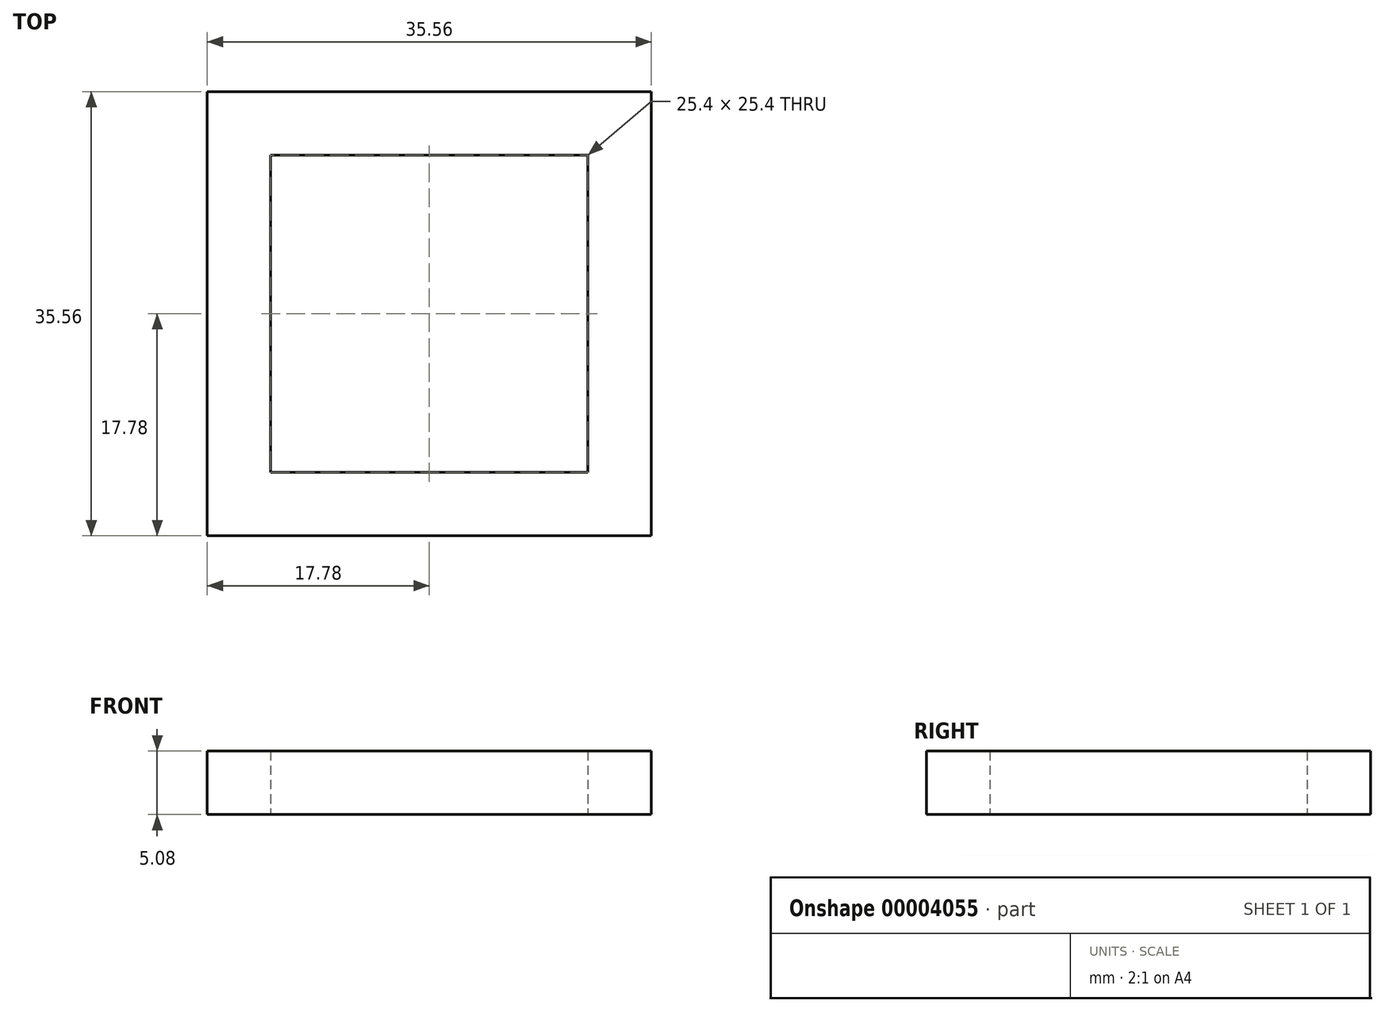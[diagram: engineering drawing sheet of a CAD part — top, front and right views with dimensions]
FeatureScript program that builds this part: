
annotation { "Feature Type Name" : "Feature", "Feature Type Description" : "" }
export const myFeature = defineFeature(function(context is Context, id is Id, definition is map)
    precondition{}
    {
        {
            var Q0;
            Q0=qCreatedBy(makeId("Top.planeOp"),FACE);
            var sketch = newSketch(context, id + "F0", { "sketchPlane" : qUnion([Q0])});
            skLineSegment(sketch, "E0.rect.bottom", {"start": v(12.7, -12.7) * mm, "end": v(-12.7, -12.7) * mm});
            skLineSegment(sketch, "E0.rect.top", {"start": v(12.7, 12.7) * mm, "end": v(-12.7, 12.7) * mm});
            skLineSegment(sketch, "E0.rect.left", {"start": v(12.7, -12.7) * mm, "end": v(12.7, 12.7) * mm});
            skLineSegment(sketch, "E0.rect.right", {"start": v(-12.7, -12.7) * mm, "end": v(-12.7, 12.7) * mm});
            skPoint(sketch, "E0.rect.middle", {"position": v(0, 0) * mm});
            skLineSegment(sketch, "E1.0", {"start": v(17.78, -17.78) * mm, "end": v(17.78, 17.78) * mm});
            skLineSegment(sketch, "E1.1", {"start": v(17.78, -17.78) * mm, "end": v(-17.78, -17.78) * mm});
            skLineSegment(sketch, "E1.2", {"start": v(-17.78, -17.78) * mm, "end": v(-17.78, 17.78) * mm});
            skLineSegment(sketch, "E1.3", {"start": v(17.78, 17.78) * mm, "end": v(-17.78, 17.78) * mm});
            skSolve(sketch);
        }
        {
            var Q0;
            Q0 = qSketchRegion(id + "F0", true);
            extrude(context, id + "F1", {"entities" : qUnion([Q0]), "depth" : 5.08 * mm});
        }
    });
